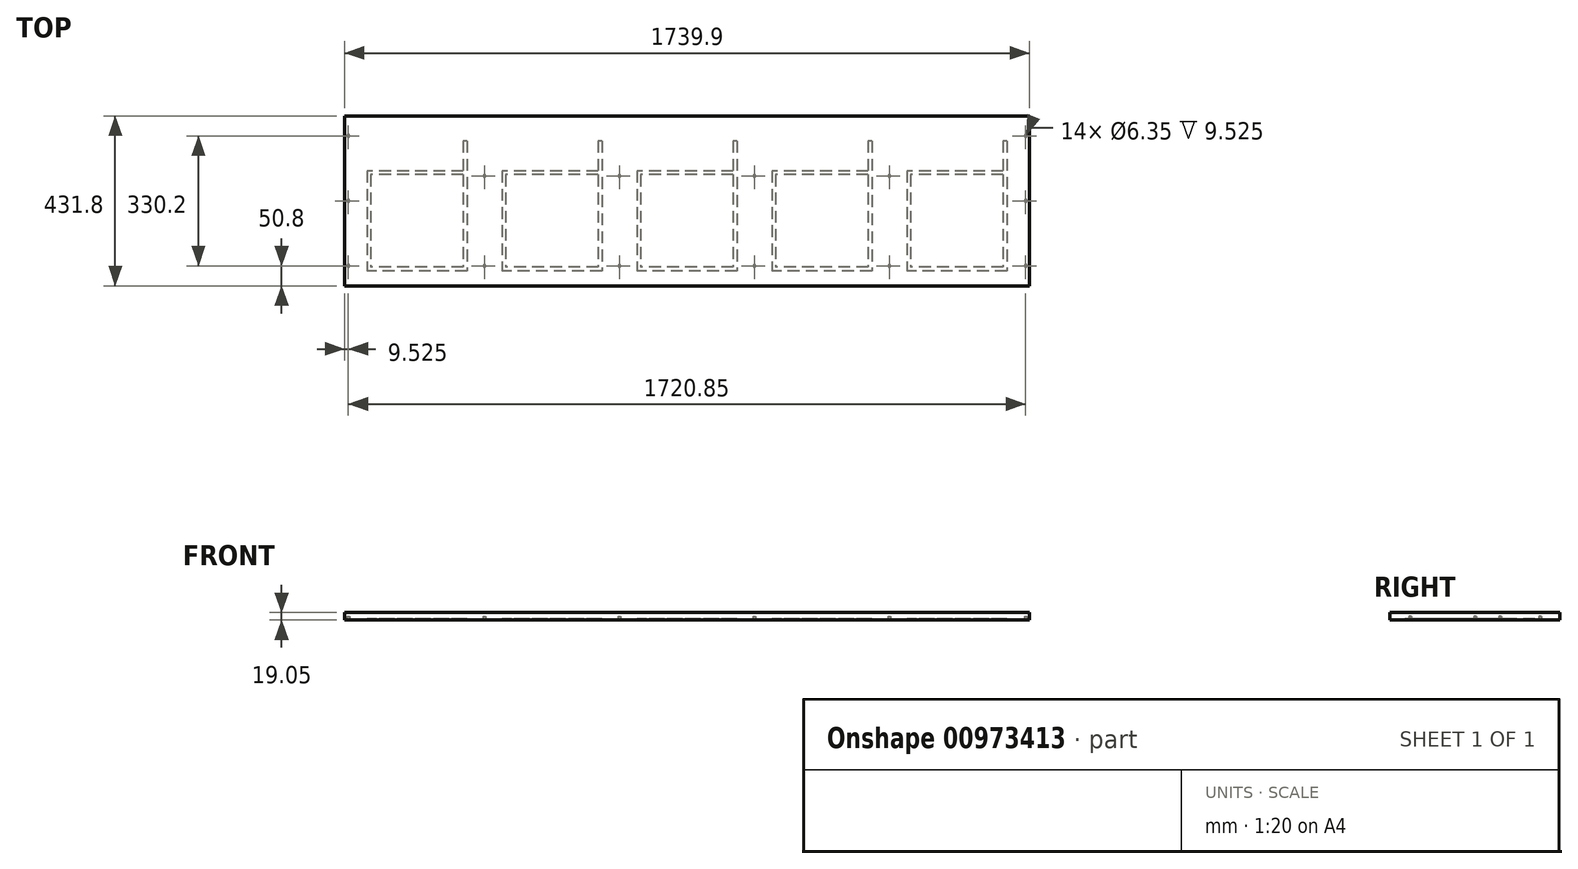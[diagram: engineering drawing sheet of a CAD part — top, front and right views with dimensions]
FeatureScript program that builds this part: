
annotation { "Feature Type Name" : "Feature", "Feature Type Description" : "" }
export const myFeature = defineFeature(function(context is Context, id is Id, definition is map)
    precondition{}
    {
        {
            var Q0;
            Q0=qCreatedBy(makeId("Front.planeOp"),FACE);
            var sketch = newSketch(context, id + "F0", { "sketchPlane" : qUnion([Q0])});
            skLineSegment(sketch, "E0.bottom", {"start": v(0, 19.05) * mm, "end": v(1739.9, 19.05) * mm});
            skLineSegment(sketch, "E0.top", {"start": v(0, 0) * mm, "end": v(1739.9, 0) * mm});
            skLineSegment(sketch, "E0.left", {"start": v(0, 19.05) * mm, "end": v(0, 0) * mm});
            skLineSegment(sketch, "E0.right", {"start": v(1739.9, 19.05) * mm, "end": v(1739.9, 0) * mm});
            skSolve(sketch);
        }
        {
            var Q0;
            Q0=qSketchRegion(id+"F0",true);
            extrude(context, id + "F1", {"entities" : qUnion([Q0]), "oppositeDirection" : true, "depth" : 431.8 * mm, "offsetDistance" : 25.4 * mm});
        }
        {
            var Q0;
            Q0=makeQuery(id+"F1.opExtrude","SWEPT_FACE",FACE,{"disambiguationData":[OSD([sQuery(id+"F0.wireOp",EDGE,"E0.top")])]});
            var sketch = newSketch(context, id + "F2", { "sketchPlane" : qUnion([Q0])});
            skCircle(sketch, "E1", {"center": v(1730.38, -381) * mm, "radius": 3.18 * mm});
            skCircle(sketch, "E2", {"center": v(1730.38, -215.9) * mm, "radius": 3.18 * mm});
            skCircle(sketch, "E3", {"center": v(1730.38, -50.8) * mm, "radius": 3.18 * mm});
            skCircle(sketch, "E4", {"center": v(9.53, -381) * mm, "radius": 3.18 * mm});
            skCircle(sketch, "E5", {"center": v(9.53, -215.9) * mm, "radius": 3.18 * mm});
            skCircle(sketch, "E6", {"center": v(9.52, -50.8) * mm, "radius": 3.18 * mm});
            skCircle(sketch, "E7", {"center": v(1384.3, -50.8) * mm, "radius": 3.18 * mm});
            skCircle(sketch, "E8", {"center": v(1384.3, -279.4) * mm, "radius": 3.18 * mm});
            skCircle(sketch, "E9", {"center": v(698.5, -50.8) * mm, "radius": 3.18 * mm});
            skCircle(sketch, "E10", {"center": v(355.6, -279.4) * mm, "radius": 3.18 * mm});
            skCircle(sketch, "E11", {"center": v(698.5, -279.4) * mm, "radius": 3.18 * mm});
            skCircle(sketch, "E12", {"center": v(1041.4, -50.8) * mm, "radius": 3.18 * mm});
            skCircle(sketch, "E13", {"center": v(1041.4, -279.4) * mm, "radius": 3.18 * mm});
            skCircle(sketch, "E14", {"center": v(355.6, -50.8) * mm, "radius": 3.18 * mm});
            skSolve(sketch);
        }
        {
            var Q0;
            Q0 = qSketchRegion(id + "F2", true);
            extrude(context, id + "F3", {"entities" : qUnion([Q0]), "operationType" : NewBodyOperationType.REMOVE, "oppositeDirection" : true, "depth" : 9.52 * mm, "offsetDistance" : 25.4 * mm});
        }
        {
            var Q0;
            Q0=makeQuery(id+"F1.opExtrude","SWEPT_FACE",FACE,{"disambiguationData":[OSD([sQuery(id+"F0.wireOp",EDGE,"E0.top")])]});
            var sketch = newSketch(context, id + "F4", { "sketchPlane" : qUnion([Q0])});
            skLineSegment(sketch, "E15.bottom", {"start": v(1682.75, -292.1) * mm, "end": v(1428.75, -292.1) * mm});
            skLineSegment(sketch, "E15.top", {"start": v(1682.75, -38.1) * mm, "end": v(1428.75, -38.1) * mm});
            skLineSegment(sketch, "E15.left", {"start": v(1682.75, -292.1) * mm, "end": v(1682.75, -38.1) * mm});
            skLineSegment(sketch, "E15.right", {"start": v(1428.75, -292.1) * mm, "end": v(1428.75, -38.1) * mm});
            skLineSegment(sketch, "E16.bottom", {"start": v(1673.23, -282.58) * mm, "end": v(1438.28, -282.58) * mm});
            skLineSegment(sketch, "E16.top", {"start": v(1673.23, -47.62) * mm, "end": v(1438.28, -47.63) * mm});
            skLineSegment(sketch, "E16.left", {"start": v(1673.23, -282.57) * mm, "end": v(1673.23, -47.62) * mm});
            skLineSegment(sketch, "E16.right", {"start": v(1438.28, -282.58) * mm, "end": v(1438.28, -47.63) * mm});
            skLineSegment(sketch, "E17.bottom", {"start": v(1339.85, -292.1) * mm, "end": v(1085.85, -292.1) * mm});
            skLineSegment(sketch, "E17.top", {"start": v(1339.85, -38.1) * mm, "end": v(1085.85, -38.1) * mm});
            skLineSegment(sketch, "E17.left", {"start": v(1339.85, -292.1) * mm, "end": v(1339.85, -38.1) * mm});
            skLineSegment(sketch, "E17.right", {"start": v(1085.85, -292.1) * mm, "end": v(1085.85, -38.1) * mm});
            skLineSegment(sketch, "E18.bottom", {"start": v(1330.33, -282.58) * mm, "end": v(1095.38, -282.58) * mm});
            skLineSegment(sketch, "E18.top", {"start": v(1330.33, -47.63) * mm, "end": v(1095.38, -47.63) * mm});
            skLineSegment(sketch, "E18.left", {"start": v(1330.33, -282.58) * mm, "end": v(1330.33, -47.63) * mm});
            skLineSegment(sketch, "E18.right", {"start": v(1095.38, -282.58) * mm, "end": v(1095.38, -47.63) * mm});
            skLineSegment(sketch, "E19.bottom", {"start": v(996.95, -292.1) * mm, "end": v(742.95, -292.1) * mm});
            skLineSegment(sketch, "E19.top", {"start": v(996.95, -38.1) * mm, "end": v(742.95, -38.1) * mm});
            skLineSegment(sketch, "E19.left", {"start": v(996.95, -292.1) * mm, "end": v(996.95, -38.1) * mm});
            skLineSegment(sketch, "E19.right", {"start": v(742.95, -292.1) * mm, "end": v(742.95, -38.1) * mm});
            skLineSegment(sketch, "E20.bottom", {"start": v(987.43, -282.58) * mm, "end": v(752.48, -282.58) * mm});
            skLineSegment(sketch, "E20.top", {"start": v(987.43, -47.63) * mm, "end": v(752.48, -47.63) * mm});
            skLineSegment(sketch, "E20.left", {"start": v(987.43, -282.58) * mm, "end": v(987.43, -47.63) * mm});
            skLineSegment(sketch, "E20.right", {"start": v(752.48, -282.58) * mm, "end": v(752.48, -47.63) * mm});
            skLineSegment(sketch, "E21.bottom", {"start": v(654.05, -292.1) * mm, "end": v(400.05, -292.1) * mm});
            skLineSegment(sketch, "E21.top", {"start": v(654.05, -38.1) * mm, "end": v(400.05, -38.1) * mm});
            skLineSegment(sketch, "E21.left", {"start": v(654.05, -292.1) * mm, "end": v(654.05, -38.1) * mm});
            skLineSegment(sketch, "E21.right", {"start": v(400.05, -292.1) * mm, "end": v(400.05, -38.1) * mm});
            skLineSegment(sketch, "E22.bottom", {"start": v(644.53, -282.58) * mm, "end": v(409.58, -282.58) * mm});
            skLineSegment(sketch, "E22.top", {"start": v(644.53, -47.63) * mm, "end": v(409.58, -47.63) * mm});
            skLineSegment(sketch, "E22.left", {"start": v(644.53, -282.57) * mm, "end": v(644.53, -47.62) * mm});
            skLineSegment(sketch, "E22.right", {"start": v(409.58, -282.58) * mm, "end": v(409.58, -47.62) * mm});
            skLineSegment(sketch, "E23.bottom", {"start": v(311.15, -292.1) * mm, "end": v(57.15, -292.1) * mm});
            skLineSegment(sketch, "E23.top", {"start": v(311.15, -38.1) * mm, "end": v(57.15, -38.1) * mm});
            skLineSegment(sketch, "E23.left", {"start": v(311.15, -292.1) * mm, "end": v(311.15, -38.1) * mm});
            skLineSegment(sketch, "E23.right", {"start": v(57.15, -292.1) * mm, "end": v(57.15, -38.1) * mm});
            skLineSegment(sketch, "E24.bottom", {"start": v(301.63, -282.58) * mm, "end": v(66.68, -282.58) * mm});
            skLineSegment(sketch, "E24.top", {"start": v(301.63, -47.63) * mm, "end": v(66.68, -47.63) * mm});
            skLineSegment(sketch, "E24.left", {"start": v(301.63, -282.57) * mm, "end": v(301.63, -47.63) * mm});
            skLineSegment(sketch, "E24.right", {"start": v(66.68, -282.58) * mm, "end": v(66.68, -47.63) * mm});
            skLineSegment(sketch, "E25.bottom", {"start": v(1682.75, -368.3) * mm, "end": v(1673.23, -368.3) * mm});
            skLineSegment(sketch, "E25.top", {"start": v(1682.75, -292.1) * mm, "end": v(1673.23, -292.1) * mm});
            skLineSegment(sketch, "E25.left", {"start": v(1682.75, -368.3) * mm, "end": v(1682.75, -292.1) * mm});
            skLineSegment(sketch, "E25.right", {"start": v(1673.23, -368.3) * mm, "end": v(1673.23, -292.1) * mm});
            skLineSegment(sketch, "E26.bottom", {"start": v(1339.85, -368.3) * mm, "end": v(1330.33, -368.3) * mm});
            skLineSegment(sketch, "E26.top", {"start": v(1339.85, -292.1) * mm, "end": v(1330.33, -292.1) * mm});
            skLineSegment(sketch, "E26.left", {"start": v(1339.85, -368.3) * mm, "end": v(1339.85, -292.1) * mm});
            skLineSegment(sketch, "E26.right", {"start": v(1330.33, -368.3) * mm, "end": v(1330.33, -292.1) * mm});
            skLineSegment(sketch, "E27.bottom", {"start": v(996.95, -368.3) * mm, "end": v(987.43, -368.3) * mm});
            skLineSegment(sketch, "E27.top", {"start": v(996.95, -292.1) * mm, "end": v(987.43, -292.1) * mm});
            skLineSegment(sketch, "E27.left", {"start": v(996.95, -368.3) * mm, "end": v(996.95, -292.1) * mm});
            skLineSegment(sketch, "E27.right", {"start": v(987.43, -368.3) * mm, "end": v(987.43, -292.1) * mm});
            skLineSegment(sketch, "E28.bottom", {"start": v(654.05, -368.3) * mm, "end": v(644.53, -368.3) * mm});
            skLineSegment(sketch, "E28.top", {"start": v(654.05, -292.1) * mm, "end": v(644.53, -292.1) * mm});
            skLineSegment(sketch, "E28.left", {"start": v(654.05, -368.3) * mm, "end": v(654.05, -292.1) * mm});
            skLineSegment(sketch, "E28.right", {"start": v(644.53, -368.3) * mm, "end": v(644.53, -292.1) * mm});
            skLineSegment(sketch, "E29.bottom", {"start": v(311.15, -368.3) * mm, "end": v(301.63, -368.3) * mm});
            skLineSegment(sketch, "E29.top", {"start": v(311.15, -292.1) * mm, "end": v(301.63, -292.1) * mm});
            skLineSegment(sketch, "E29.left", {"start": v(311.15, -368.3) * mm, "end": v(311.15, -292.1) * mm});
            skLineSegment(sketch, "E29.right", {"start": v(301.63, -368.3) * mm, "end": v(301.63, -292.1) * mm});
            skSolve(sketch);
        }
        {
            var Q0;
            Q0 = qSketchRegion(id + "F4", true);
            extrude(context, id + "F5", {"entities" : qUnion([Q0]), "operationType" : NewBodyOperationType.REMOVE, "oppositeDirection" : true, "depth" : 3.17 * mm, "offsetDistance" : 25.4 * mm});
        }
    });
